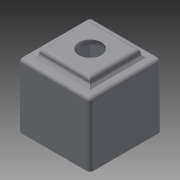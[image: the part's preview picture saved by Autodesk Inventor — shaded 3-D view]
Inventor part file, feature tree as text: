
AUTODESK INVENTOR PART (.ipt)
format: ipt  version: 2014 (Build 180170000, 170)  size: 231,936 bytes
history: native  units: in
note: dims shown in document units (in); Inventor stores cm internally (conversion verified against a paired STEP export)
features: sketch x9, extrude x8, fillet x2, revolve x1, chamfer x1
ambient origin geometry x8: Origin, YZ Plane, XZ Plane, XY Plane, X Axis, Y Axis, Z Axis, Center Point
bodies: Solid1 (feature_tree)
feature tree (21):
  extrude  "Extrusion1"  Depth=2.7in
  extrude  "Extrusion2"  Depth=0.1in
  extrude  "Extrusion3"  Depth=0.1in
  extrude  "Extrusion4"  Depth=2.3in TaperAngle=0.0deg
  revolve  "Revolution1"  [1 undecoded]
  extrude  "Extrusion5"  Depth=0.4in
  extrude  "Extrusion6"  Depth=0.29in
  extrude  "Extrusion7"  Depth=0.7812in
  chamfer  "Chamfer1"  Distance=0.1875in
  fillet  "Fillet1"  Radius=0.9375in
  extrude  "Extrusion8"  Depth=0.4688in
  fillet  "Fillet2"  Radius=0.9375in
  sketch  "Sketch1"  dims[d2=2.7in d3=2.7in]
  sketch  "Sketch2"  dims[d4=2.4in d5=0.0in d6=0.1in]
  sketch  "Sketch3"  dims[d7=0.1in d8=0.1in]
  sketch  "Sketch4"  dims[d9=0.1in d10=2.3in d11=0.0in]
  sketch  "Sketch5"  dims[d12=0.4in d13=0.4in]
  sketch  "Sketch6"  dims[d14=0.4in d15=0.4in]
  sketch  "Sketch7"  dims[d16=0.29in d17=0.0in d18=0.9375in]
  sketch  "Sketch8"  dims[d19=0.9375in d20=0.7812in]
  sketch  "Sketch9"  dims[d21=0.7812in d22=0.1875in d23=0.0in d24=0.9375in d25=0.4688in d26=0.9375in d27=90.0deg d28=0.1in d29=0.1in d30=0.1in d31=0.3in d32=0.1in d33=0.1in d34=0.3in d35=0.1in d36=0.1in d37=0.1in d38=0.1in d39=2.6in d40=0.0in d41=2.6in d42=0.0in d43=2.6in d44=0.0in d45=0.1in d46=0.125in d47=45.0deg d48=0.125in d49=0.5in d51=0.5in d52=0.5in d53=0.5in d54=0.1875in d55=0.0in d56=0.125in]
note: 1 required parameter value undecoded (feature->parameter linkage not recoverable at this tier; creation-order binding heuristic only, values carry confidence <= 0.55)
